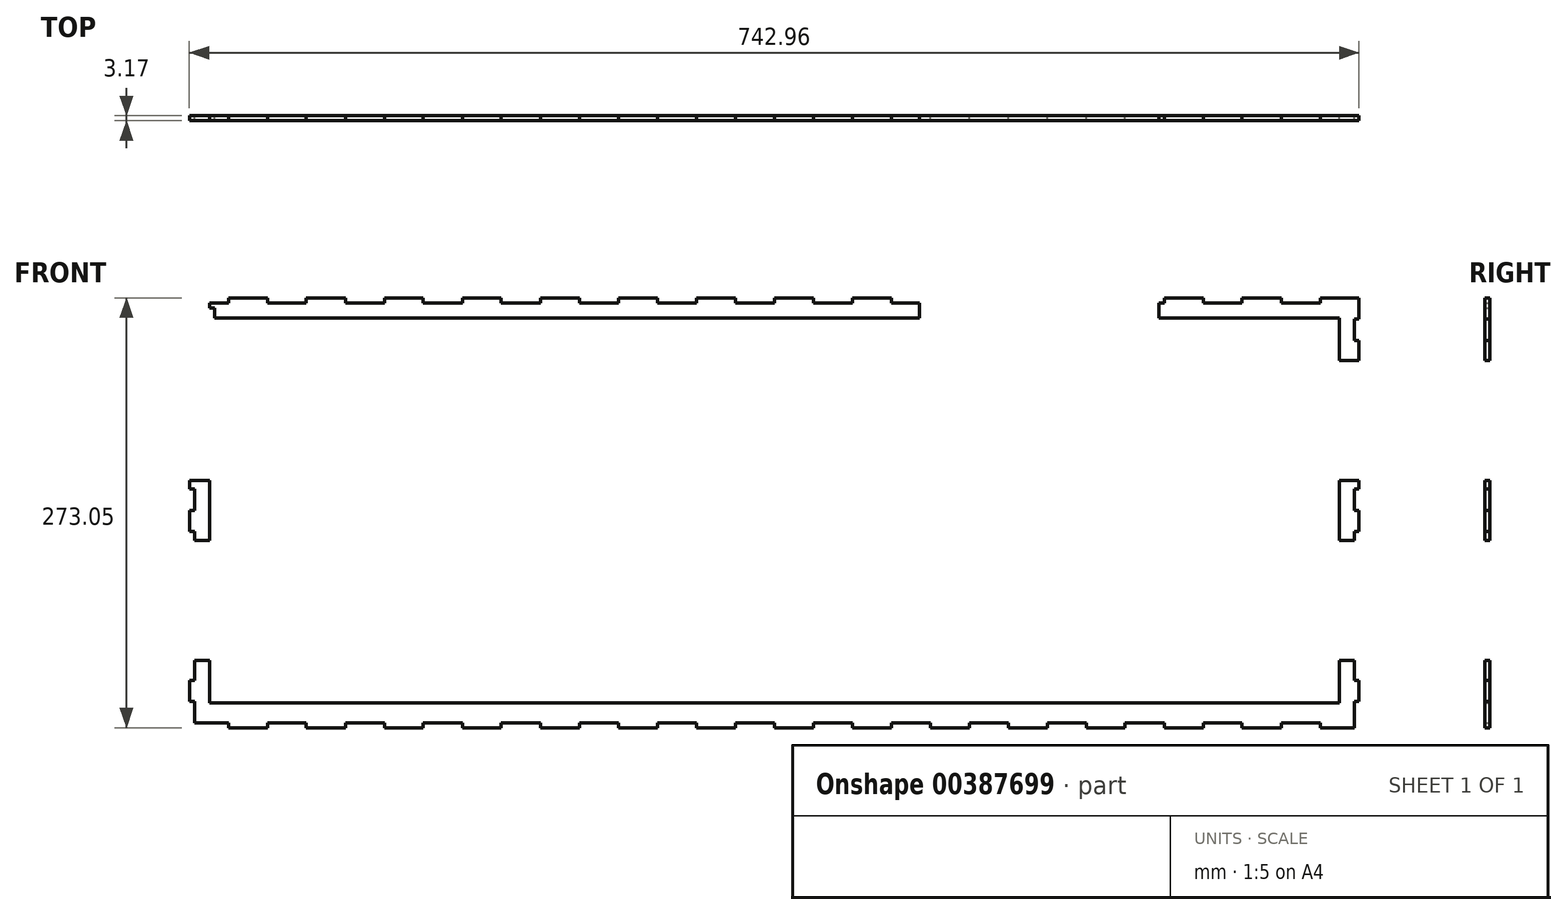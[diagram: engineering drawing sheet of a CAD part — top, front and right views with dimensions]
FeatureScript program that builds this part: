
annotation { "Feature Type Name" : "Feature", "Feature Type Description" : "" }
export const myFeature = defineFeature(function(context is Context, id is Id, definition is map)
    precondition{}
    {
        {
            var Q0;
            Q0=qCreatedBy(makeId("Front.planeOp"),FACE);
            var sketch = newSketch(context, id + "F0", { "sketchPlane" : qUnion([Q0])});
            skPoint(sketch, "E0.middle", {"position": v(0, 0) * mm});
            skLineSegment(sketch, "E1.bottom", {"start": v(358.77, -122.24) * mm, "end": v(-358.78, -122.24) * mm});
            skLineSegment(sketch, "E1.top", {"start": v(358.78, 122.24) * mm, "end": v(-358.77, 122.24) * mm});
            skLineSegment(sketch, "E1.left", {"start": v(358.77, -122.24) * mm, "end": v(358.78, 122.24) * mm});
            skLineSegment(sketch, "E1.right", {"start": v(-358.78, -122.24) * mm, "end": v(-358.78, 122.24) * mm});
            skLineSegment(sketch, "E2", {"start": v(0, 0) * mm, "end": v(-371.48, 0) * mm, "construction": true});
            skLineSegment(sketch, "E3", {"start": v(-371.48, 0) * mm, "end": v(0, 0) * mm, "construction": true});
            skLineSegment(sketch, "E4", {"start": v(0, 0) * mm, "end": v(371.48, 0) * mm, "construction": true});
            skLineSegment(sketch, "E5", {"start": v(0, -0.7) * mm, "end": v(0, -134.94) * mm, "construction": true});
            skLineSegment(sketch, "E6.bottom", {"start": v(-358.77, 122.24) * mm, "end": v(-355.6, 122.24) * mm});
            skLineSegment(sketch, "E6.top", {"start": v(-358.78, 128.59) * mm, "end": v(-355.6, 128.59) * mm});
            skLineSegment(sketch, "E6.right", {"start": v(-355.6, 122.24) * mm, "end": v(-355.6, 128.59) * mm});
            skLineSegment(sketch, "E7", {"start": v(0, 0) * mm, "end": v(-75.73, -75.73) * mm, "construction": true});
            skLineSegment(sketch, "E8", {"start": v(-75.73, -75.73) * mm, "end": v(0, -75.73) * mm, "construction": true});
            skLineSegment(sketch, "E9.MirrorCS", {"start": v(358.78, 128.59) * mm, "end": v(355.6, 128.59) * mm});
            skLineSegment(sketch, "E10.MirrorCS", {"start": v(355.6, 122.24) * mm, "end": v(355.6, 128.59) * mm});
            skLineSegment(sketch, "E11.MirrorCS", {"start": v(355.6, -122.24) * mm, "end": v(355.6, -128.59) * mm});
            skLineSegment(sketch, "E12.MirrorCS", {"start": v(358.78, -128.59) * mm, "end": v(355.6, -128.59) * mm});
            skLineSegment(sketch, "E13.MirrorCS", {"start": v(-355.6, -122.24) * mm, "end": v(-355.6, -128.59) * mm});
            skLineSegment(sketch, "E14.MirrorCS", {"start": v(-358.78, -128.59) * mm, "end": v(-355.6, -128.59) * mm});
            skLineSegment(sketch, "E15.MirrorCS", {"start": v(371.48, 134.94) * mm, "end": v(371.48, 121.44) * mm});
            skLineSegment(sketch, "E16.MirrorCS", {"start": v(371.48, 121.44) * mm, "end": v(368.3, 121.44) * mm});
            skLineSegment(sketch, "E17.MirrorCS", {"start": v(368.3, 121.44) * mm, "end": v(368.3, 107.95) * mm});
            skLineSegment(sketch, "E18.MirrorCS", {"start": v(371.47, 107.95) * mm, "end": v(368.3, 107.95) * mm});
            skLineSegment(sketch, "E19.MirrorCS", {"start": v(371.47, 13.5) * mm, "end": v(368.3, 13.5) * mm});
            skLineSegment(sketch, "E20.MirrorCS", {"start": v(368.3, 13.5) * mm, "end": v(368.3, 0) * mm});
            skLineSegment(sketch, "E21.MirrorCS", {"start": v(371.47, 0) * mm, "end": v(371.47, -13.5) * mm});
            skLineSegment(sketch, "E22.MirrorCS", {"start": v(371.47, -13.5) * mm, "end": v(368.3, -13.5) * mm});
            skLineSegment(sketch, "E23.MirrorCS", {"start": v(371.47, -107.95) * mm, "end": v(368.3, -107.95) * mm});
            skLineSegment(sketch, "E24.MirrorCS", {"start": v(371.47, -107.95) * mm, "end": v(371.47, -121.44) * mm});
            skLineSegment(sketch, "E25.MirrorCS", {"start": v(371.47, -121.44) * mm, "end": v(368.3, -121.44) * mm});
            skLineSegment(sketch, "E26.MirrorCS", {"start": v(368.3, -121.44) * mm, "end": v(368.3, -134.94) * mm});
            skLineSegment(sketch, "E27", {"start": v(368.3, 0) * mm, "end": v(371.48, 0) * mm});
            skLineSegment(sketch, "E28", {"start": v(358.78, -128.59) * mm, "end": v(358.78, -134.94) * mm});
            skLineSegment(sketch, "E29", {"start": v(358.78, 128.59) * mm, "end": v(358.78, 134.94) * mm});
            skLineSegment(sketch, "E30.right", {"start": v(-346.7, -138.11) * mm, "end": v(-346.71, -134.94) * mm});
            skLineSegment(sketch, "E31.1.0.2", {"start": v(-321.95, -138.11) * mm, "end": v(-321.95, -134.94) * mm});
            skLineSegment(sketch, "E31.2.0.0", {"start": v(-321.95, -138.11) * mm, "end": v(-321.95, -134.94) * mm});
            skLineSegment(sketch, "E31.2.0.1", {"start": v(-321.95, -134.94) * mm, "end": v(-297.18, -134.94) * mm});
            skLineSegment(sketch, "E31.2.0.2", {"start": v(-297.18, -138.11) * mm, "end": v(-297.18, -134.94) * mm});
            skLineSegment(sketch, "E31.3.0.0", {"start": v(-297.18, -138.11) * mm, "end": v(-297.18, -134.94) * mm});
            skLineSegment(sketch, "E31.3.0.2", {"start": v(-272.42, -138.11) * mm, "end": v(-272.42, -134.94) * mm});
            skLineSegment(sketch, "E31.4.0.0", {"start": v(-272.42, -138.11) * mm, "end": v(-272.42, -134.94) * mm});
            skLineSegment(sketch, "E31.4.0.1", {"start": v(-272.42, -134.94) * mm, "end": v(-247.65, -134.94) * mm});
            skLineSegment(sketch, "E31.4.0.2", {"start": v(-247.65, -138.11) * mm, "end": v(-247.65, -134.94) * mm});
            skLineSegment(sketch, "E31.5.0.0", {"start": v(-247.65, -138.11) * mm, "end": v(-247.65, -134.94) * mm});
            skLineSegment(sketch, "E31.5.0.2", {"start": v(-222.89, -138.11) * mm, "end": v(-222.89, -134.94) * mm});
            skLineSegment(sketch, "E31.6.0.0", {"start": v(-222.89, -138.11) * mm, "end": v(-222.89, -134.94) * mm});
            skLineSegment(sketch, "E31.6.0.1", {"start": v(-222.89, -134.94) * mm, "end": v(-198.12, -134.94) * mm});
            skLineSegment(sketch, "E31.6.0.2", {"start": v(-198.12, -138.11) * mm, "end": v(-198.12, -134.94) * mm});
            skLineSegment(sketch, "E31.7.0.0", {"start": v(-198.12, -138.11) * mm, "end": v(-198.12, -134.94) * mm});
            skLineSegment(sketch, "E31.7.0.2", {"start": v(-173.36, -138.11) * mm, "end": v(-173.36, -134.94) * mm});
            skLineSegment(sketch, "E31.8.0.0", {"start": v(-173.36, -138.11) * mm, "end": v(-173.36, -134.94) * mm});
            skLineSegment(sketch, "E31.8.0.1", {"start": v(-173.36, -134.94) * mm, "end": v(-148.6, -134.94) * mm});
            skLineSegment(sketch, "E31.8.0.2", {"start": v(-148.6, -138.11) * mm, "end": v(-148.6, -134.94) * mm});
            skLineSegment(sketch, "E31.9.0.0", {"start": v(-148.6, -138.11) * mm, "end": v(-148.6, -134.94) * mm});
            skLineSegment(sketch, "E31.9.0.2", {"start": v(-123.83, -138.11) * mm, "end": v(-123.83, -134.94) * mm});
            skLineSegment(sketch, "E31.10.0.0", {"start": v(-123.83, -138.11) * mm, "end": v(-123.83, -134.94) * mm});
            skLineSegment(sketch, "E31.10.0.1", {"start": v(-123.83, -134.94) * mm, "end": v(-99.06, -134.94) * mm});
            skLineSegment(sketch, "E31.10.0.2", {"start": v(-99.06, -138.11) * mm, "end": v(-99.06, -134.94) * mm});
            skLineSegment(sketch, "E31.11.0.0", {"start": v(-99.06, -138.11) * mm, "end": v(-99.06, -134.94) * mm});
            skLineSegment(sketch, "E31.11.0.2", {"start": v(-74.3, -138.11) * mm, "end": v(-74.3, -134.94) * mm});
            skLineSegment(sketch, "E31.12.0.0", {"start": v(-74.3, -138.11) * mm, "end": v(-74.3, -134.94) * mm});
            skLineSegment(sketch, "E31.12.0.1", {"start": v(-74.3, -134.94) * mm, "end": v(-49.53, -134.94) * mm});
            skLineSegment(sketch, "E31.12.0.2", {"start": v(-49.53, -138.11) * mm, "end": v(-49.53, -134.94) * mm});
            skLineSegment(sketch, "E31.13.0.0", {"start": v(-49.53, -138.11) * mm, "end": v(-49.53, -134.94) * mm});
            skLineSegment(sketch, "E31.13.0.2", {"start": v(-24.77, -138.11) * mm, "end": v(-24.77, -134.94) * mm});
            skLineSegment(sketch, "E31.14.0.0", {"start": v(-24.77, -138.11) * mm, "end": v(-24.77, -134.94) * mm});
            skLineSegment(sketch, "E31.14.0.1", {"start": v(-24.77, -134.94) * mm, "end": v(0, -134.94) * mm});
            skLineSegment(sketch, "E31.14.0.2", {"start": v(0, -138.11) * mm, "end": v(0, -134.94) * mm});
            skLineSegment(sketch, "E31.15.0.0", {"start": v(0, -138.11) * mm, "end": v(0, -134.94) * mm});
            skLineSegment(sketch, "E31.15.0.2", {"start": v(24.76, -138.11) * mm, "end": v(24.76, -134.94) * mm});
            skLineSegment(sketch, "E31.16.0.0", {"start": v(24.76, -138.11) * mm, "end": v(24.76, -134.94) * mm});
            skLineSegment(sketch, "E31.16.0.1", {"start": v(24.76, -134.94) * mm, "end": v(49.53, -134.94) * mm});
            skLineSegment(sketch, "E31.16.0.2", {"start": v(49.53, -138.11) * mm, "end": v(49.53, -134.94) * mm});
            skLineSegment(sketch, "E31.17.0.0", {"start": v(49.53, -138.11) * mm, "end": v(49.53, -134.94) * mm});
            skLineSegment(sketch, "E31.17.0.2", {"start": v(74.3, -138.11) * mm, "end": v(74.3, -134.94) * mm});
            skLineSegment(sketch, "E31.18.0.0", {"start": v(74.3, -138.11) * mm, "end": v(74.3, -134.94) * mm});
            skLineSegment(sketch, "E31.18.0.1", {"start": v(74.3, -134.94) * mm, "end": v(99.06, -134.94) * mm});
            skLineSegment(sketch, "E31.18.0.2", {"start": v(99.06, -138.11) * mm, "end": v(99.06, -134.94) * mm});
            skLineSegment(sketch, "E31.19.0.0", {"start": v(99.06, -138.11) * mm, "end": v(99.06, -134.94) * mm});
            skLineSegment(sketch, "E31.19.0.2", {"start": v(123.82, -138.11) * mm, "end": v(123.82, -134.94) * mm});
            skLineSegment(sketch, "E31.20.0.0", {"start": v(123.82, -138.11) * mm, "end": v(123.82, -134.94) * mm});
            skLineSegment(sketch, "E31.20.0.1", {"start": v(123.82, -134.94) * mm, "end": v(148.59, -134.94) * mm});
            skLineSegment(sketch, "E31.20.0.2", {"start": v(148.59, -138.11) * mm, "end": v(148.59, -134.94) * mm});
            skLineSegment(sketch, "E31.21.0.0", {"start": v(148.59, -138.11) * mm, "end": v(148.59, -134.94) * mm});
            skLineSegment(sketch, "E31.21.0.2", {"start": v(173.35, -138.11) * mm, "end": v(173.35, -134.94) * mm});
            skLineSegment(sketch, "E31.22.0.0", {"start": v(173.35, -138.11) * mm, "end": v(173.35, -134.94) * mm});
            skLineSegment(sketch, "E31.22.0.1", {"start": v(173.35, -134.94) * mm, "end": v(198.12, -134.94) * mm});
            skLineSegment(sketch, "E31.22.0.2", {"start": v(198.12, -138.11) * mm, "end": v(198.12, -134.94) * mm});
            skLineSegment(sketch, "E31.23.0.0", {"start": v(198.12, -138.11) * mm, "end": v(198.12, -134.94) * mm});
            skLineSegment(sketch, "E31.23.0.2", {"start": v(222.88, -138.11) * mm, "end": v(222.88, -134.94) * mm});
            skLineSegment(sketch, "E31.24.0.0", {"start": v(222.88, -138.11) * mm, "end": v(222.88, -134.94) * mm});
            skLineSegment(sketch, "E31.24.0.1", {"start": v(222.88, -134.94) * mm, "end": v(247.65, -134.94) * mm});
            skLineSegment(sketch, "E31.24.0.2", {"start": v(247.65, -138.11) * mm, "end": v(247.65, -134.94) * mm});
            skLineSegment(sketch, "E31.25.0.0", {"start": v(247.65, -138.11) * mm, "end": v(247.65, -134.94) * mm});
            skLineSegment(sketch, "E31.25.0.2", {"start": v(272.41, -138.11) * mm, "end": v(272.41, -134.94) * mm});
            skLineSegment(sketch, "E31.26.0.0", {"start": v(272.41, -138.11) * mm, "end": v(272.41, -134.94) * mm});
            skLineSegment(sketch, "E31.26.0.1", {"start": v(272.41, -134.94) * mm, "end": v(297.18, -134.94) * mm});
            skLineSegment(sketch, "E31.26.0.2", {"start": v(297.18, -138.11) * mm, "end": v(297.18, -134.94) * mm});
            skLineSegment(sketch, "E31.27.0.0", {"start": v(297.18, -138.11) * mm, "end": v(297.18, -134.94) * mm});
            skLineSegment(sketch, "E31.27.0.2", {"start": v(321.94, -138.11) * mm, "end": v(321.94, -134.94) * mm});
            skLineSegment(sketch, "E31.28.0.0", {"start": v(321.94, -138.11) * mm, "end": v(321.94, -134.94) * mm});
            skLineSegment(sketch, "E31.28.0.1", {"start": v(321.94, -134.94) * mm, "end": v(346.7, -134.94) * mm});
            skLineSegment(sketch, "E31.28.0.2", {"start": v(346.7, -138.11) * mm, "end": v(346.7, -134.94) * mm});
            skLineSegment(sketch, "E32", {"start": v(-358.78, -128.59) * mm, "end": v(-358.78, -131.76) * mm});
            skLineSegment(sketch, "E33", {"start": v(-346.71, -138.11) * mm, "end": v(-321.95, -138.11) * mm});
            skLineSegment(sketch, "E34", {"start": v(-297.18, -138.11) * mm, "end": v(-272.42, -138.11) * mm});
            skLineSegment(sketch, "E35", {"start": v(-247.65, -138.11) * mm, "end": v(-222.89, -138.11) * mm});
            skLineSegment(sketch, "E36", {"start": v(-198.12, -138.11) * mm, "end": v(-173.36, -138.11) * mm});
            skLineSegment(sketch, "E37", {"start": v(-148.6, -138.11) * mm, "end": v(-123.83, -138.11) * mm});
            skLineSegment(sketch, "E38", {"start": v(-99.06, -138.11) * mm, "end": v(-74.3, -138.11) * mm});
            skLineSegment(sketch, "E39", {"start": v(-49.53, -138.11) * mm, "end": v(-24.77, -138.11) * mm});
            skLineSegment(sketch, "E40", {"start": v(0, -138.11) * mm, "end": v(24.76, -138.11) * mm});
            skLineSegment(sketch, "E41", {"start": v(49.53, -138.11) * mm, "end": v(74.3, -138.11) * mm});
            skLineSegment(sketch, "E42", {"start": v(99.06, -138.11) * mm, "end": v(123.82, -138.11) * mm});
            skLineSegment(sketch, "E43", {"start": v(148.59, -138.11) * mm, "end": v(173.35, -138.11) * mm});
            skLineSegment(sketch, "E44", {"start": v(198.12, -138.11) * mm, "end": v(222.88, -138.11) * mm});
            skLineSegment(sketch, "E45", {"start": v(247.65, -138.11) * mm, "end": v(272.41, -138.11) * mm});
            skLineSegment(sketch, "E46", {"start": v(297.18, -138.11) * mm, "end": v(321.94, -138.11) * mm});
            skLineSegment(sketch, "E47.MirrorCS", {"start": v(-346.7, 134.94) * mm, "end": v(-346.7, 131.76) * mm});
            skLineSegment(sketch, "E48.MirrorCS", {"start": v(-346.7, 134.94) * mm, "end": v(-321.94, 134.94) * mm});
            skLineSegment(sketch, "E49.MirrorCS", {"start": v(-321.94, 134.94) * mm, "end": v(-321.94, 131.76) * mm});
            skLineSegment(sketch, "E50.MirrorCS", {"start": v(-321.94, 131.76) * mm, "end": v(-297.18, 131.76) * mm});
            skLineSegment(sketch, "E51.MirrorCS", {"start": v(-297.18, 134.94) * mm, "end": v(-297.18, 131.76) * mm});
            skLineSegment(sketch, "E52.MirrorCS", {"start": v(-297.18, 134.94) * mm, "end": v(-272.42, 134.94) * mm});
            skLineSegment(sketch, "E53.MirrorCS", {"start": v(-272.42, 134.94) * mm, "end": v(-272.42, 131.76) * mm});
            skLineSegment(sketch, "E54.MirrorCS", {"start": v(-272.42, 131.76) * mm, "end": v(-247.65, 131.76) * mm});
            skLineSegment(sketch, "E55.MirrorCS", {"start": v(-247.65, 134.94) * mm, "end": v(-247.65, 131.76) * mm});
            skLineSegment(sketch, "E56.MirrorCS", {"start": v(-247.65, 134.94) * mm, "end": v(-222.89, 134.94) * mm});
            skLineSegment(sketch, "E57.MirrorCS", {"start": v(-222.89, 134.94) * mm, "end": v(-222.89, 131.76) * mm});
            skLineSegment(sketch, "E58.MirrorCS", {"start": v(-222.89, 131.76) * mm, "end": v(-198.12, 131.76) * mm});
            skLineSegment(sketch, "E59.MirrorCS", {"start": v(-198.12, 134.94) * mm, "end": v(-198.12, 131.76) * mm});
            skLineSegment(sketch, "E60.MirrorCS", {"start": v(-198.12, 134.94) * mm, "end": v(-173.36, 134.94) * mm});
            skLineSegment(sketch, "E61.MirrorCS", {"start": v(-173.36, 134.94) * mm, "end": v(-173.36, 131.76) * mm});
            skLineSegment(sketch, "E62.MirrorCS", {"start": v(-173.36, 131.76) * mm, "end": v(-148.6, 131.76) * mm});
            skLineSegment(sketch, "E63.MirrorCS", {"start": v(-148.6, 134.94) * mm, "end": v(-148.6, 131.76) * mm});
            skLineSegment(sketch, "E64.MirrorCS", {"start": v(-148.6, 134.94) * mm, "end": v(-123.83, 134.94) * mm});
            skLineSegment(sketch, "E65.MirrorCS", {"start": v(-123.83, 134.94) * mm, "end": v(-123.83, 131.76) * mm});
            skLineSegment(sketch, "E66.MirrorCS", {"start": v(-123.83, 131.76) * mm, "end": v(-99.06, 131.76) * mm});
            skLineSegment(sketch, "E67.MirrorCS", {"start": v(-99.06, 134.94) * mm, "end": v(-99.06, 131.76) * mm});
            skLineSegment(sketch, "E68.MirrorCS", {"start": v(-99.06, 134.94) * mm, "end": v(-74.3, 134.94) * mm});
            skLineSegment(sketch, "E69.MirrorCS", {"start": v(-74.3, 134.94) * mm, "end": v(-74.3, 131.76) * mm});
            skLineSegment(sketch, "E70.MirrorCS", {"start": v(-74.3, 131.76) * mm, "end": v(-49.53, 131.76) * mm});
            skLineSegment(sketch, "E71.MirrorCS", {"start": v(-49.53, 134.94) * mm, "end": v(-49.53, 131.76) * mm});
            skLineSegment(sketch, "E72.MirrorCS", {"start": v(-49.53, 134.94) * mm, "end": v(-24.77, 134.94) * mm});
            skLineSegment(sketch, "E73.MirrorCS", {"start": v(-24.77, 134.94) * mm, "end": v(-24.77, 131.76) * mm});
            skLineSegment(sketch, "E74.MirrorCS", {"start": v(-24.77, 131.76) * mm, "end": v(0, 131.76) * mm});
            skLineSegment(sketch, "E75.MirrorCS", {"start": v(0, 0.7) * mm, "end": v(0, 134.94) * mm, "construction": true});
            skLineSegment(sketch, "E76.MirrorCS", {"start": v(0, 134.94) * mm, "end": v(24.76, 134.94) * mm});
            skLineSegment(sketch, "E77.MirrorCS", {"start": v(24.76, 134.94) * mm, "end": v(24.76, 131.76) * mm});
            skLineSegment(sketch, "E78.MirrorCS", {"start": v(24.76, 131.76) * mm, "end": v(49.53, 131.76) * mm});
            skLineSegment(sketch, "E79.MirrorCS", {"start": v(49.53, 134.94) * mm, "end": v(49.53, 131.76) * mm});
            skLineSegment(sketch, "E80.MirrorCS", {"start": v(49.53, 134.94) * mm, "end": v(74.3, 134.94) * mm});
            skLineSegment(sketch, "E81.MirrorCS", {"start": v(74.3, 134.94) * mm, "end": v(74.3, 131.76) * mm});
            skLineSegment(sketch, "E82.MirrorCS", {"start": v(247.65, 134.94) * mm, "end": v(247.65, 131.76) * mm});
            skLineSegment(sketch, "E83.MirrorCS", {"start": v(247.65, 134.94) * mm, "end": v(272.41, 134.94) * mm});
            skLineSegment(sketch, "E84.MirrorCS", {"start": v(272.41, 134.94) * mm, "end": v(272.41, 131.76) * mm});
            skLineSegment(sketch, "E85.MirrorCS", {"start": v(272.41, 131.76) * mm, "end": v(297.18, 131.76) * mm});
            skLineSegment(sketch, "E86.MirrorCS", {"start": v(297.18, 134.94) * mm, "end": v(297.18, 131.76) * mm});
            skLineSegment(sketch, "E87.MirrorCS", {"start": v(321.94, 134.94) * mm, "end": v(321.94, 131.76) * mm});
            skLineSegment(sketch, "E88.MirrorCS", {"start": v(321.94, 131.76) * mm, "end": v(346.7, 131.76) * mm});
            skLineSegment(sketch, "E89", {"start": v(0, 134.94) * mm, "end": v(0, 131.76) * mm});
            skLineSegment(sketch, "E90", {"start": v(-346.7, 131.76) * mm, "end": v(-371.48, 131.76) * mm});
            skLineSegment(sketch, "E91", {"start": v(-371.48, 121.44) * mm, "end": v(-371.48, 131.76) * mm});
            skLineSegment(sketch, "E92", {"start": v(-358.78, 128.59) * mm, "end": v(-358.78, 131.76) * mm});
            skPoint(sketch, "E93.endSnap0", {"position": v(37.15, -134.94) * mm});
            skLineSegment(sketch, "E94", {"start": v(-371.47, -134.94) * mm, "end": v(-371.47, -151.81) * mm});
            skLineSegment(sketch, "E95", {"start": v(-371.47, -151.81) * mm, "end": v(92.08, -151.81) * mm, "construction": true});
            skLineSegment(sketch, "E96", {"start": v(92.08, -151.81) * mm, "end": v(244.48, -151.81) * mm, "construction": true});
            skLineSegment(sketch, "E97", {"start": v(244.48, -151.81) * mm, "end": v(371.47, -151.81) * mm, "construction": true});
            skLineSegment(sketch, "E98", {"start": v(74.3, 131.76) * mm, "end": v(92.08, 131.76) * mm});
            skLineSegment(sketch, "E99", {"start": v(92.08, 131.76) * mm, "end": v(92.08, 134.94) * mm, "construction": true});
            skLineSegment(sketch, "E100", {"start": v(92.08, 134.94) * mm, "end": v(74.3, 134.94) * mm, "construction": true});
            skLineSegment(sketch, "E101", {"start": v(247.65, 131.76) * mm, "end": v(244.48, 131.76) * mm});
            skLineSegment(sketch, "E102", {"start": v(92.08, 131.76) * mm, "end": v(92.08, 122.24) * mm});
            skLineSegment(sketch, "E103", {"start": v(244.48, 131.76) * mm, "end": v(244.48, 122.24) * mm});
            skLineSegment(sketch, "E104", {"start": v(368.3, -134.94) * mm, "end": v(421.5, -134.94) * mm, "construction": true});
            skLineSegment(sketch, "E105.MirrorCS", {"start": v(407.76, -134.94) * mm, "end": v(407.76, 134.94) * mm, "construction": true});
            skLineSegment(sketch, "E106", {"start": v(412.82, -134.94) * mm, "end": v(412.82, -95.25) * mm});
            skLineSegment(sketch, "E107", {"start": v(412.82, -95.25) * mm, "end": v(412.82, -19.05) * mm});
            skLineSegment(sketch, "E108", {"start": v(412.82, -19.05) * mm, "end": v(412.82, 19.05) * mm});
            skLineSegment(sketch, "E109", {"start": v(412.82, 19.05) * mm, "end": v(412.82, 95.25) * mm});
            skLineSegment(sketch, "E110", {"start": v(412.82, 95.25) * mm, "end": v(412.82, 134.94) * mm});
            skLineSegment(sketch, "E111", {"start": v(412.82, -19.05) * mm, "end": v(334.18, -19.05) * mm, "construction": true});
            skLineSegment(sketch, "E112", {"start": v(412.82, 19.05) * mm, "end": v(334.72, 19.05) * mm, "construction": true});
            skLineSegment(sketch, "E113", {"start": v(412.82, 95.25) * mm, "end": v(342.67, 95.25) * mm, "construction": true});
            skLineSegment(sketch, "E114", {"start": v(368.3, -13.5) * mm, "end": v(368.3, -19.05) * mm});
            skLineSegment(sketch, "E115", {"start": v(368.3, -107.95) * mm, "end": v(368.3, -95.25) * mm});
            skLineSegment(sketch, "E116", {"start": v(371.47, 13.5) * mm, "end": v(371.47, 19.05) * mm});
            skLineSegment(sketch, "E117", {"start": v(371.47, 107.95) * mm, "end": v(371.47, 95.25) * mm});
            skLineSegment(sketch, "E118", {"start": v(368.3, -19.05) * mm, "end": v(358.78, -19.05) * mm});
            skLineSegment(sketch, "E119", {"start": v(371.47, 19.05) * mm, "end": v(358.78, 19.05) * mm});
            skLineSegment(sketch, "E120", {"start": v(371.47, 95.25) * mm, "end": v(358.78, 95.25) * mm});
            skLineSegment(sketch, "E121.MirrorCS", {"start": v(-371.47, 121.44) * mm, "end": v(-368.3, 121.44) * mm});
            skLineSegment(sketch, "E122.MirrorCS", {"start": v(-368.3, 121.44) * mm, "end": v(-368.3, 107.95) * mm});
            skLineSegment(sketch, "E123.MirrorCS", {"start": v(-371.47, 107.95) * mm, "end": v(-368.3, 107.95) * mm});
            skLineSegment(sketch, "E124.MirrorCS", {"start": v(-371.47, 107.95) * mm, "end": v(-371.47, 95.25) * mm});
            skLineSegment(sketch, "E125.MirrorCS", {"start": v(-371.47, 13.5) * mm, "end": v(-371.47, 19.05) * mm});
            skLineSegment(sketch, "E126.MirrorCS", {"start": v(-371.47, 13.5) * mm, "end": v(-368.3, 13.5) * mm});
            skLineSegment(sketch, "E127.MirrorCS", {"start": v(-368.3, 13.5) * mm, "end": v(-368.3, 0) * mm});
            skLineSegment(sketch, "E128.MirrorCS", {"start": v(-371.47, 0) * mm, "end": v(-371.47, -13.5) * mm});
            skLineSegment(sketch, "E129.MirrorCS", {"start": v(-371.47, -13.5) * mm, "end": v(-368.3, -13.5) * mm});
            skLineSegment(sketch, "E130.MirrorCS", {"start": v(-368.3, -13.5) * mm, "end": v(-368.3, -19.05) * mm});
            skLineSegment(sketch, "E131.MirrorCS", {"start": v(-368.3, -107.95) * mm, "end": v(-368.3, -95.25) * mm});
            skLineSegment(sketch, "E132.MirrorCS", {"start": v(-371.47, -107.95) * mm, "end": v(-368.3, -107.95) * mm});
            skLineSegment(sketch, "E133.MirrorCS", {"start": v(-371.47, -107.95) * mm, "end": v(-371.47, -121.44) * mm});
            skLineSegment(sketch, "E134.MirrorCS", {"start": v(-371.47, -121.44) * mm, "end": v(-368.3, -121.44) * mm});
            skLineSegment(sketch, "E135", {"start": v(-371.47, 19.05) * mm, "end": v(-358.78, 19.05) * mm});
            skLineSegment(sketch, "E136", {"start": v(-371.47, 95.25) * mm, "end": v(-358.78, 95.25) * mm});
            skLineSegment(sketch, "E137", {"start": v(-368.3, -19.05) * mm, "end": v(-358.78, -19.05) * mm});
            skLineSegment(sketch, "E138", {"start": v(-368.3, -121.44) * mm, "end": v(-368.3, -131.76) * mm});
            skLineSegment(sketch, "E139", {"start": v(-368.3, 0) * mm, "end": v(-371.48, 0) * mm});
            skLineSegment(sketch, "E140", {"start": v(358.78, 134.94) * mm, "end": v(371.48, 134.94) * mm});
            skLineSegment(sketch, "E141", {"start": v(-358.78, -134.94) * mm, "end": v(-349.89, -134.94) * mm});
            skLineSegment(sketch, "E142", {"start": v(358.78, -138.11) * mm, "end": v(349.88, -138.11) * mm});
            skLineSegment(sketch, "E143", {"start": v(365.12, -138.11) * mm, "end": v(358.78, -138.11) * mm});
            skLineSegment(sketch, "E144", {"start": v(365.12, -95.25) * mm, "end": v(358.77, -95.25) * mm});
            skLineSegment(sketch, "E145", {"start": v(365.12, -138.11) * mm, "end": v(368.3, -138.11) * mm});
            skLineSegment(sketch, "E146", {"start": v(365.12, -95.25) * mm, "end": v(368.3, -95.25) * mm});
            skLineSegment(sketch, "E147", {"start": v(-358.78, -134.94) * mm, "end": v(-365.12, -134.94) * mm});
            skLineSegment(sketch, "E148", {"start": v(-365.12, -95.25) * mm, "end": v(-358.78, -95.25) * mm});
            skLineSegment(sketch, "E149", {"start": v(-368.3, -95.25) * mm, "end": v(-365.12, -95.25) * mm});
            skLineSegment(sketch, "E150", {"start": v(-368.3, -134.94) * mm, "end": v(-365.12, -134.94) * mm});
            skLineSegment(sketch, "E151", {"start": v(297.18, 134.94) * mm, "end": v(318.77, 134.94) * mm});
            skLineSegment(sketch, "E152", {"start": v(346.7, 131.76) * mm, "end": v(346.7, 134.94) * mm});
            skLineSegment(sketch, "E153", {"start": v(318.77, 134.94) * mm, "end": v(321.94, 134.94) * mm});
            skLineSegment(sketch, "E154", {"start": v(346.7, 134.94) * mm, "end": v(358.78, 134.94) * mm});
            skLineSegment(sketch, "E155", {"start": v(-368.3, -131.76) * mm, "end": v(-368.3, -134.94) * mm});
            skLineSegment(sketch, "E156", {"start": v(-358.78, -131.76) * mm, "end": v(-358.78, -134.94) * mm});
            skLineSegment(sketch, "E157", {"start": v(358.78, -134.94) * mm, "end": v(358.78, -138.11) * mm});
            skLineSegment(sketch, "E158", {"start": v(368.3, -134.94) * mm, "end": v(368.3, -138.11) * mm});
            skLineSegment(sketch, "E159", {"start": v(-349.89, -134.94) * mm, "end": v(-346.71, -134.94) * mm});
            skLineSegment(sketch, "E160", {"start": v(346.7, -138.11) * mm, "end": v(349.88, -138.11) * mm});
            skSolve(sketch);
        }
        {
            var Q0;
            Q0=makeQuery(id+"F0.imprint","IMPRINT",FACE,{"disambiguationData":[TD([[makeQuery(id+"F0.imprint","IMPRINT",EDGE,{"derivedFrom":sQuery(id+"F0.wireOp",EDGE,"E19.MirrorCS")}),-1.0]])]});
            var Q1;
            Q1=makeQuery(id+"F0.imprint","IMPRINT",FACE,{"disambiguationData":[TD([[makeQuery(id+"F0.imprint","IMPRINT",EDGE,{"derivedFrom":sQuery(id+"F0.wireOp",EDGE,"E125.MirrorCS")}),-1.0]])]});
            var Q2;
            {var subQ7=sQuery(id+"F0.wireOp",EDGE,"E11.MirrorCS");Q2=makeQuery(id+"F0.imprint","IMPRINT",FACE,{"disambiguationData":[TD([[makeQuery(id+"F0.imprint","IMPRINT",EDGE,{"derivedFrom":subQ7}),1.0]])]});}
            var Q3;
            {var subQ4=sQuery(id+"F0.wireOp",EDGE,"E13.MirrorCS");Q3=makeQuery(id+"F0.imprint","IMPRINT",FACE,{"disambiguationData":[TD([[makeQuery(id+"F0.imprint","IMPRINT",EDGE,{"derivedFrom":subQ4}),-1.0]])]});}
            var Q4;
            Q4=makeQuery(id+"F0.imprint","IMPRINT",FACE,{"disambiguationData":[TD([[makeQuery(id+"F0.imprint","IMPRINT",EDGE,{"derivedFrom":sQuery(id+"F0.wireOp",EDGE,"E9.MirrorCS")}),1.0]])]});
            var Q5;
            Q5=makeQuery(id+"F0.imprint","IMPRINT",FACE,{"disambiguationData":[TD([[makeQuery(id+"F0.imprint","IMPRINT",EDGE,{"derivedFrom":sQuery(id+"F0.wireOp",EDGE,"E9.MirrorCS")}),-1.0]])]});
            var Q6;
            Q6=makeQuery(id+"F0.imprint","IMPRINT",FACE,{"disambiguationData":[TD([[makeQuery(id+"F0.imprint","IMPRINT",EDGE,{"derivedFrom":sQuery(id+"F0.wireOp",EDGE,"E6.top")}),1.0]])]});
            var Q7;
            {var subQ1=sQuery(id+"F0.wireOp",EDGE,"E6.bottom");Q7=makeQuery(id+"F0.imprint","IMPRINT",FACE,{"disambiguationData":[TD([[makeQuery(id+"F0.imprint","IMPRINT",EDGE,{"derivedFrom":subQ1}),1.0]])]});}
            var Q8;
            {var subQ1=sQuery(id+"F0.wireOp",EDGE,"E11.MirrorCS");Q8=makeQuery(id+"F0.imprint","IMPRINT",FACE,{"disambiguationData":[TD([[makeQuery(id+"F0.imprint","IMPRINT",EDGE,{"derivedFrom":subQ1}),-1.0]])]});}
            extrude(context, id + "F1", {"entities" : qUnion([Q0, Q1, Q2, Q3, Q4, Q5, Q6, Q7, Q8]), "depth" : 3.17 * mm});
        }
    });
